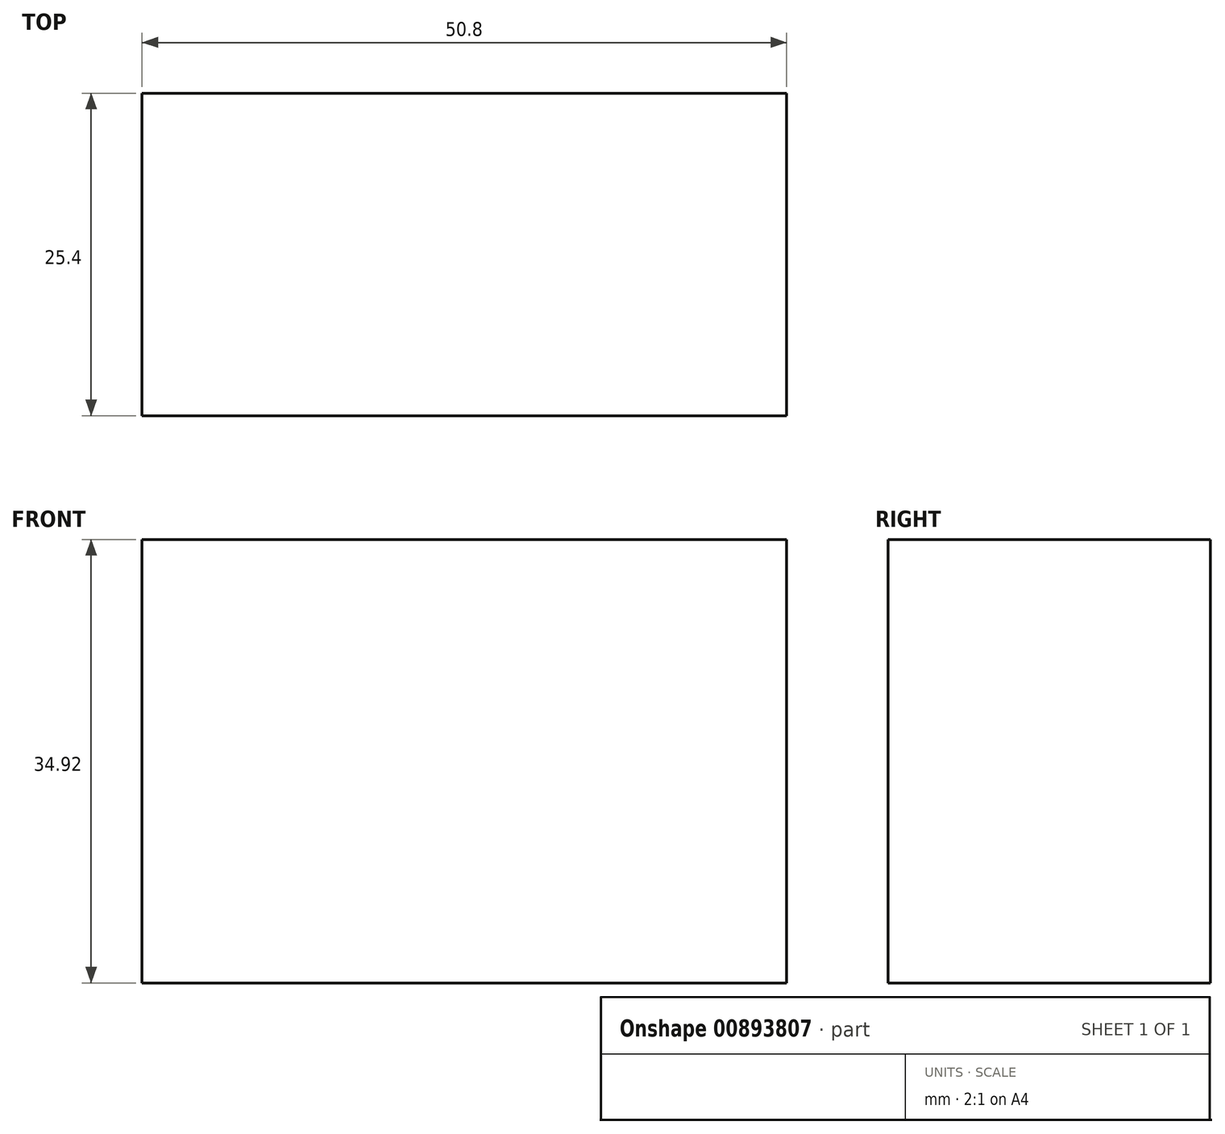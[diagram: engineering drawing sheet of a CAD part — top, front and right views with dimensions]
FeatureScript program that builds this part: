
annotation { "Feature Type Name" : "Feature", "Feature Type Description" : "" }
export const myFeature = defineFeature(function(context is Context, id is Id, definition is map)
    precondition{}
    {
        {
            var Q0;
            Q0=qCreatedBy(makeId("Top.planeOp"),FACE);
            var sketch = newSketch(context, id + "F0", { "sketchPlane" : qUnion([Q0])});
            skLineSegment(sketch, "E0.bottom", {"start": v(-25.4, 12.7) * mm, "end": v(25.4, 12.7) * mm});
            skLineSegment(sketch, "E0.top", {"start": v(-25.4, -12.7) * mm, "end": v(25.4, -12.7) * mm});
            skLineSegment(sketch, "E0.left", {"start": v(-25.4, 12.7) * mm, "end": v(-25.4, -12.7) * mm});
            skLineSegment(sketch, "E0.right", {"start": v(25.4, 12.7) * mm, "end": v(25.4, -12.7) * mm});
            skPoint(sketch, "E0.middle", {"position": v(0, 0) * mm});
            skSolve(sketch);
        }
        {
            var Q0;
            Q0 = qSketchRegion(id + "F0", true);
            extrude(context, id + "F1", {"entities" : qUnion([Q0]), "depth" : 34.92 * mm, "offsetDistance" : 25.4 * mm});
        }
    });
